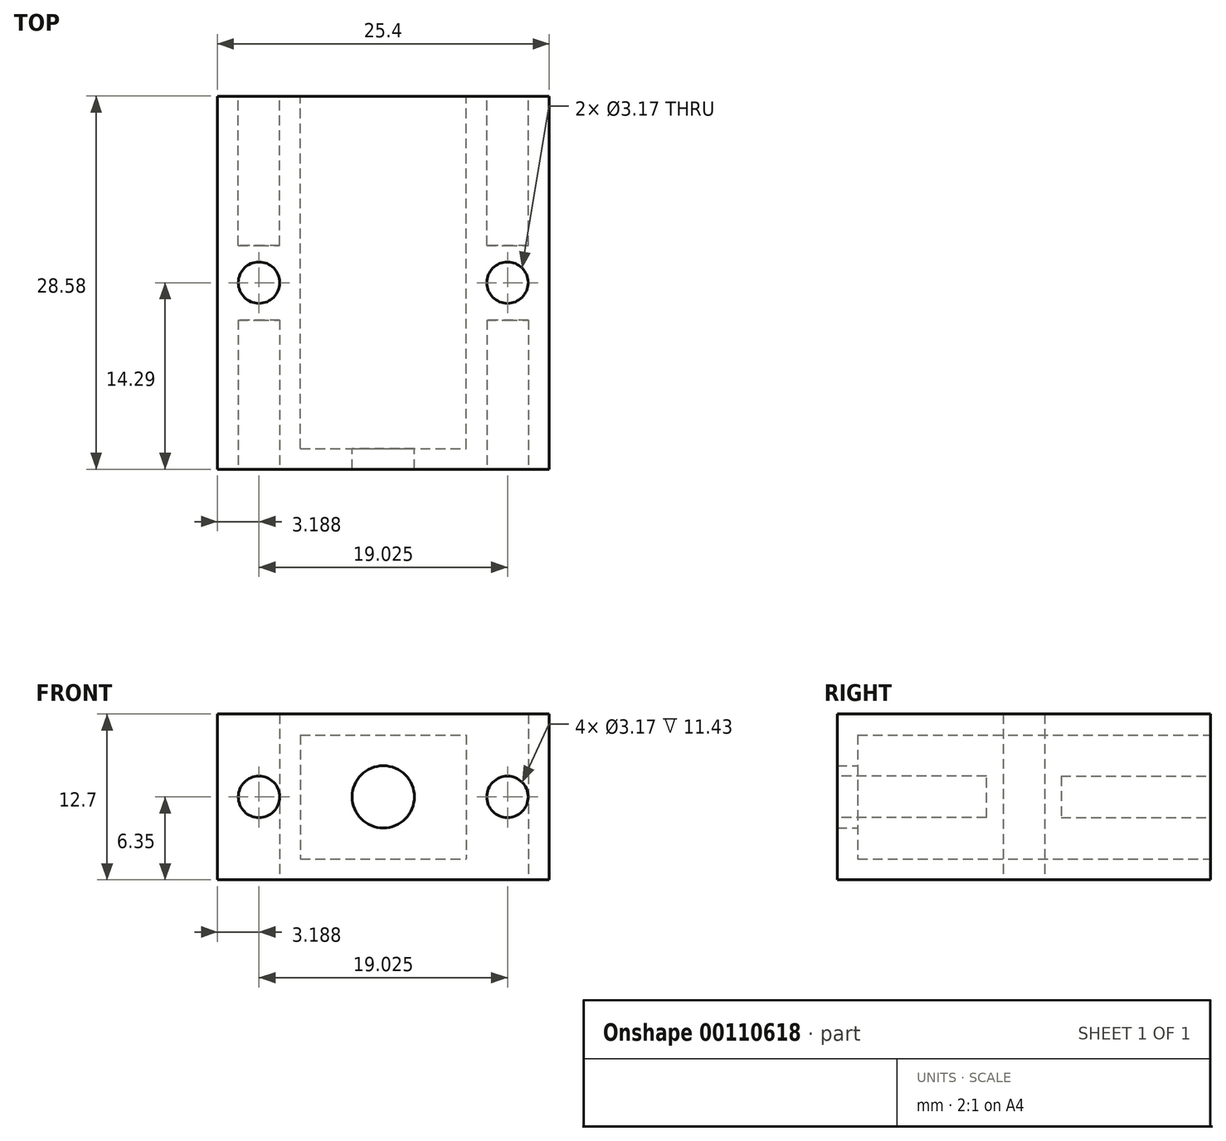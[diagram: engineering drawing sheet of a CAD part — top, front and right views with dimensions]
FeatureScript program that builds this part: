
annotation { "Feature Type Name" : "Feature", "Feature Type Description" : "" }
export const myFeature = defineFeature(function(context is Context, id is Id, definition is map)
    precondition{}
    {
        {
            var Q0;
            Q0=qCreatedBy(makeId("Top.planeOp"),FACE);
            var sketch = newSketch(context, id + "F0", { "sketchPlane" : qUnion([Q0])});
            skLineSegment(sketch, "E0.rect.bottom", {"start": v(12.7, 14.29) * mm, "end": v(-12.7, 14.29) * mm});
            skLineSegment(sketch, "E0.rect.top", {"start": v(12.7, -14.29) * mm, "end": v(-12.7, -14.29) * mm});
            skLineSegment(sketch, "E0.rect.left", {"start": v(12.7, 14.29) * mm, "end": v(12.7, -14.29) * mm});
            skLineSegment(sketch, "E0.rect.right", {"start": v(-12.7, 14.29) * mm, "end": v(-12.7, -14.29) * mm});
            skPoint(sketch, "E0.rect.middle", {"position": v(0, 0) * mm});
            skCircle(sketch, "E1", {"center": v(-9.51, 0) * mm, "radius": 1.59 * mm});
            skCircle(sketch, "E2", {"center": v(9.51, 0) * mm, "radius": 1.59 * mm});
            skSolve(sketch);
        }
        {
            var Q0;
            Q0=qSketchRegion(id+"F0",true);
            extrude(context, id + "F1", {"entities" : qUnion([Q0]), "depth" : 12.7 * mm});
        }
        {
            var Q0;
            Q0=makeQuery(id+"F1.opExtrude","SWEPT_FACE",FACE,{"disambiguationData":[OSD([sQuery(id+"F0.wireOp",EDGE,"E0.rect.bottom")])]});
            var sketch = newSketch(context, id + "F2", { "sketchPlane" : qUnion([Q0])});
            skLineSegment(sketch, "E3.rect.bottom", {"start": v(6.35, 11.1) * mm, "end": v(-6.35, 11.1) * mm});
            skLineSegment(sketch, "E3.rect.top", {"start": v(6.35, 1.6) * mm, "end": v(-6.35, 1.6) * mm});
            skLineSegment(sketch, "E3.rect.left", {"start": v(6.35, 11.1) * mm, "end": v(6.35, 1.6) * mm});
            skLineSegment(sketch, "E3.rect.right", {"start": v(-6.35, 11.1) * mm, "end": v(-6.35, 1.6) * mm});
            skPoint(sketch, "E3.rect.middle", {"position": v(0, 6.35) * mm});
            skSolve(sketch);
        }
        {
            var Q0;
            Q0=qSketchRegion(id+"F2",true);
            extrude(context, id + "F3", {"entities" : qUnion([Q0]), "operationType" : NewBodyOperationType.REMOVE, "oppositeDirection" : true, "depth" : 27 * mm});
        }
        {
            var Q0;
            Q0=makeQuery(id+"F3.boolean.opBoolean","COPY",FACE,{"derivedFrom":makeQuery(id+"F3.opExtrude","CAP_FACE",FACE,{"disambiguationData":[OSD([sQuery(id+"F2.wireOp",EDGE,"E3.rect.bottom"),sQuery(id+"F2.wireOp",EDGE,"E3.rect.top"),sQuery(id+"F2.wireOp",EDGE,"E3.rect.left"),sQuery(id+"F2.wireOp",EDGE,"E3.rect.right")])],"isStart":false})});
            var sketch = newSketch(context, id + "F4", { "sketchPlane" : qUnion([Q0])});
            skCircle(sketch, "E4", {"center": v(0, 6.35) * mm, "radius": 2.38 * mm});
            skPoint(sketch, "E5", {"position": v(6.35, 6.35) * mm});
            skSolve(sketch);
        }
        {
            var Q0;
            Q0=qSketchRegion(id+"F4",true);
            extrude(context, id + "F5", {"entities" : qUnion([Q0]), "operationType" : NewBodyOperationType.REMOVE, "endBound" : BoundingType.THROUGH_ALL, "oppositeDirection" : true, "depth" : 25.4 * mm});
        }
        {
            var Q0;
            Q0=makeQuery(id+"F1.opExtrude","SWEPT_FACE",FACE,{"disambiguationData":[OSD([sQuery(id+"F0.wireOp",EDGE,"E0.rect.top")])]});
            var sketch = newSketch(context, id + "F6", { "sketchPlane" : qUnion([Q0])});
            skPoint(sketch, "E6", {"position": v(0, 6.35) * mm});
            skCircle(sketch, "E7", {"center": v(-9.51, 6.35) * mm, "radius": 1.59 * mm});
            skCircle(sketch, "E8", {"center": v(9.51, 6.35) * mm, "radius": 1.59 * mm});
            skSolve(sketch);
        }
        {
            var Q0;
            Q0=qSketchRegion(id+"F6",true);
            extrude(context, id + "F7", {"entities" : qUnion([Q0]), "operationType" : NewBodyOperationType.REMOVE, "oppositeDirection" : true, "depth" : 11.43 * mm});
        }
        {
            var Q0;
            Q0=makeQuery(id+"F1.opExtrude","SWEPT_FACE",FACE,{"disambiguationData":[OSD([sQuery(id+"F0.wireOp",EDGE,"E0.rect.bottom")])]});
            var sketch = newSketch(context, id + "F8", { "sketchPlane" : qUnion([Q0])});
            skCircle(sketch, "E9", {"center": v(-9.51, 6.35) * mm, "radius": 1.59 * mm});
            skPoint(sketch, "E9.centerSnap0", {"position": v(-6.35, 6.35) * mm});
            skCircle(sketch, "E10", {"center": v(9.51, 6.35) * mm, "radius": 1.59 * mm});
            skPoint(sketch, "E10.centerSnap0", {"position": v(6.35, 6.35) * mm});
            skSolve(sketch);
        }
        {
            var Q0;
            Q0=qSketchRegion(id+"F8",true);
            extrude(context, id + "F9", {"entities" : qUnion([Q0]), "operationType" : NewBodyOperationType.REMOVE, "oppositeDirection" : true, "depth" : 11.43 * mm});
        }
    });
